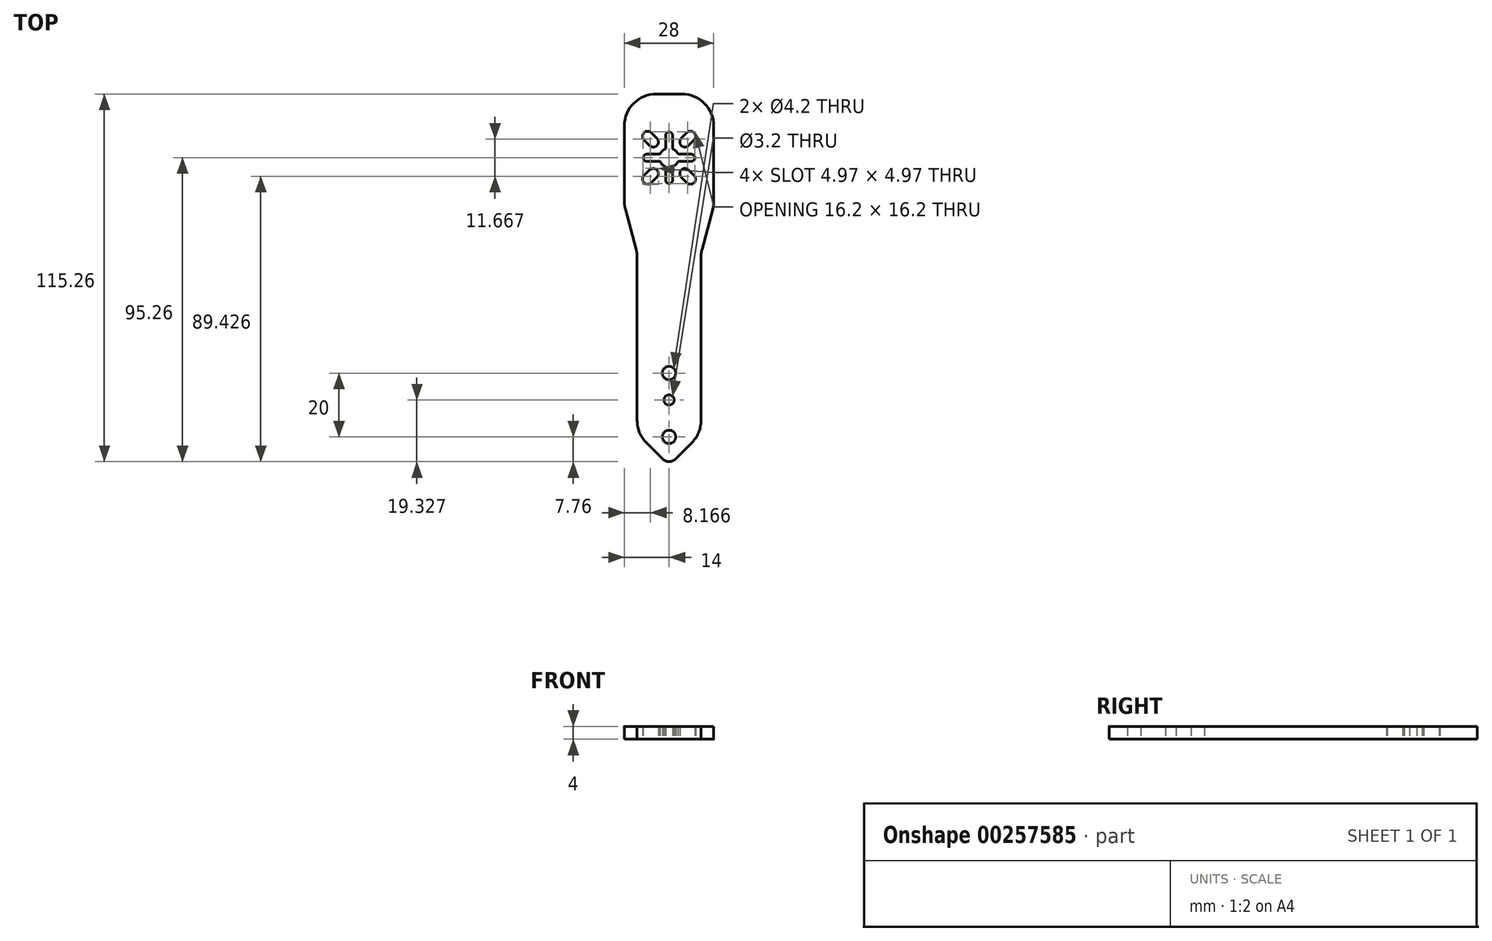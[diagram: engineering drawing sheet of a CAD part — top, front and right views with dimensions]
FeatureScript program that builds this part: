
annotation { "Feature Type Name" : "Feature", "Feature Type Description" : "" }
export const myFeature = defineFeature(function(context is Context, id is Id, definition is map)
    precondition{}
    {
        {
            var Q0;
            Q0=qCreatedBy(makeId("Top.planeOp"),FACE);
            var sketch = newSketch(context, id + "F0", { "sketchPlane" : qUnion([Q0])});
            skLineSegment(sketch, "E0", {"start": v(0, 97.5) * mm, "end": v(0, -97.5) * mm, "construction": true});
            skArc(sketch, "E1", {"start": v(2.8, 98.6) * mm, "mid": v(2.12, 99.62) * mm, "end": v(1.1, 100.3) * mm});
            skCircle(sketch, "E2", {"center": v(0, 10) * mm, "radius": 2.1 * mm});
            skCircle(sketch, "E3", {"center": v(0, 30) * mm, "radius": 2.1 * mm});
            skCircle(sketch, "E4", {"center": v(0, 21.57) * mm, "radius": 1.6 * mm});
            skArc(sketch, "E5", {"start": v(7.85, 103.09) * mm, "mid": v(7.85, 105.35) * mm, "end": v(5.59, 105.35) * mm});
            skArc(sketch, "E6", {"start": v(3.82, 103.58) * mm, "mid": v(3.82, 101.32) * mm, "end": v(6.08, 101.32) * mm});
            skLineSegment(sketch, "E7", {"start": v(5.59, 105.35) * mm, "end": v(3.82, 103.58) * mm});
            skLineSegment(sketch, "E8", {"start": v(7.85, 103.09) * mm, "end": v(6.08, 101.32) * mm});
            skLineSegment(sketch, "E9", {"start": v(0, 97.5) * mm, "end": v(6.72, 104.22) * mm, "construction": true});
            skArc(sketch, "E10", {"start": v(7, 96.4) * mm, "mid": v(8.1, 97.5) * mm, "end": v(7, 98.6) * mm});
            skLineSegment(sketch, "E11", {"start": v(7, 98.6) * mm, "end": v(2.8, 98.6) * mm});
            skLineSegment(sketch, "E12", {"start": v(0, 97.5) * mm, "end": v(7, 97.5) * mm, "construction": true});
            skLineSegment(sketch, "E13.MirrorCS", {"start": v(7, 96.4) * mm, "end": v(2.8, 96.4) * mm});
            skLineSegment(sketch, "E14.1.0", {"start": v(1.1, 104.5) * mm, "end": v(1.1, 100.3) * mm});
            skLineSegment(sketch, "E14.1.1", {"start": v(-1.1, 104.5) * mm, "end": v(-1.1, 100.3) * mm});
            skArc(sketch, "E14.1.2", {"start": v(1.1, 104.5) * mm, "mid": v(0, 105.6) * mm, "end": v(-1.1, 104.5) * mm});
            skArc(sketch, "E14.1.4", {"start": v(-5.59, 105.35) * mm, "mid": v(-7.85, 105.35) * mm, "end": v(-7.85, 103.09) * mm});
            skLineSegment(sketch, "E14.1.5", {"start": v(-7.85, 103.09) * mm, "end": v(-6.08, 101.32) * mm});
            skLineSegment(sketch, "E14.1.6", {"start": v(-5.59, 105.35) * mm, "end": v(-3.82, 103.58) * mm});
            skArc(sketch, "E14.1.7", {"start": v(-6.08, 101.32) * mm, "mid": v(-3.82, 101.32) * mm, "end": v(-3.82, 103.58) * mm});
            skLineSegment(sketch, "E14.2.0", {"start": v(-7, 98.6) * mm, "end": v(-2.8, 98.6) * mm});
            skLineSegment(sketch, "E14.2.1", {"start": v(-7, 96.4) * mm, "end": v(-2.8, 96.4) * mm});
            skArc(sketch, "E14.2.2", {"start": v(-7, 98.6) * mm, "mid": v(-8.1, 97.5) * mm, "end": v(-7, 96.4) * mm});
            skArc(sketch, "E14.2.4", {"start": v(-7.85, 91.91) * mm, "mid": v(-7.85, 89.65) * mm, "end": v(-5.59, 89.65) * mm});
            skLineSegment(sketch, "E14.2.5", {"start": v(-5.59, 89.65) * mm, "end": v(-3.82, 91.42) * mm});
            skLineSegment(sketch, "E14.2.6", {"start": v(-7.85, 91.91) * mm, "end": v(-6.08, 93.68) * mm});
            skArc(sketch, "E14.2.7", {"start": v(-3.82, 91.42) * mm, "mid": v(-3.82, 93.68) * mm, "end": v(-6.08, 93.68) * mm});
            skLineSegment(sketch, "E15.3.3.0", {"start": v(1.1, 90.5) * mm, "end": v(1.1, 94.7) * mm});
            skArc(sketch, "E15.6.3.0", {"start": v(-1.1, 90.5) * mm, "mid": v(0, 89.4) * mm, "end": v(1.1, 90.5) * mm});
            skLineSegment(sketch, "E15.11.3.0", {"start": v(-1.1, 90.5) * mm, "end": v(-1.1, 94.7) * mm});
            skArc(sketch, "E15.13.3.0", {"start": v(5.59, 89.65) * mm, "mid": v(7.85, 89.65) * mm, "end": v(7.85, 91.91) * mm});
            skLineSegment(sketch, "E15.17.3.0", {"start": v(7.85, 91.91) * mm, "end": v(6.08, 93.68) * mm});
            skLineSegment(sketch, "E15.20.3.0", {"start": v(5.59, 89.65) * mm, "end": v(3.82, 91.42) * mm});
            skArc(sketch, "E15.23.3.0", {"start": v(6.08, 93.68) * mm, "mid": v(3.82, 93.68) * mm, "end": v(3.82, 91.42) * mm});
            skArc(sketch, "E16.trimOffspring", {"start": v(-2.8, 96.4) * mm, "mid": v(-2.12, 95.38) * mm, "end": v(-1.1, 94.7) * mm});
            skArc(sketch, "E17.trimOffspring", {"start": v(-1.1, 100.3) * mm, "mid": v(-2.12, 99.62) * mm, "end": v(-2.8, 98.6) * mm});
            skArc(sketch, "E18.trimOffspring", {"start": v(1.1, 94.7) * mm, "mid": v(2.12, 95.38) * mm, "end": v(2.8, 96.4) * mm});
            skLineSegment(sketch, "E19", {"start": v(-10, 11) * mm, "end": v(-10, 67.57) * mm});
            skLineSegment(sketch, "E20", {"start": v(-10, 67.57) * mm, "end": v(-14, 82.5) * mm});
            skLineSegment(sketch, "E21", {"start": v(-14, 82.5) * mm, "end": v(-14, 117.5) * mm});
            skLineSegment(sketch, "E22.MirrorCS", {"start": v(10, 11) * mm, "end": v(10, 67.57) * mm});
            skLineSegment(sketch, "E23.MirrorCS", {"start": v(10, 67.57) * mm, "end": v(14, 82.5) * mm});
            skLineSegment(sketch, "E24.MirrorCS", {"start": v(14, 82.5) * mm, "end": v(14, 117.5) * mm});
            skLineSegment(sketch, "E25", {"start": v(-10, 11) * mm, "end": v(0, 1) * mm});
            skLineSegment(sketch, "E26", {"start": v(10, 11) * mm, "end": v(0, 1) * mm});
            skLineSegment(sketch, "E27", {"start": v(-14, 117.5) * mm, "end": v(14, 117.5) * mm});
            skCircle(sketch, "E28.MirrorC", {"center": v(0, -21.57) * mm, "radius": 1.6 * mm, "construction": true});
            skCircle(sketch, "E29", {"center": v(21.57, 0) * mm, "radius": 1.6 * mm, "construction": true});
            skLineSegment(sketch, "E30", {"start": v(0, 21.57) * mm, "end": v(21.57, 0) * mm, "construction": true});
            skLineSegment(sketch, "E31", {"start": v(21.57, 0) * mm, "end": v(0, -21.57) * mm, "construction": true});
            skSolve(sketch);
        }
        {
            var Q0;
            Q0 = qSketchRegion(id + "F0", true);
            extrude(context, id + "F1", {"entities" : qUnion([Q0]), "depth" : 4 * mm});
        }
        {
            var Q0;
            Q0=makeQuery(id+"F1.opExtrude","SWEPT_EDGE",EDGE,{"disambiguationData":[OSD([sQuery(id+"F0.wireOp",EDGE,"E20"),sQuery(id+"F0.wireOp",EDGE,"E21")])]});
            var Q1;
            Q1=makeQuery(id+"F1.opExtrude","SWEPT_EDGE",EDGE,{"disambiguationData":[OSD([sQuery(id+"F0.wireOp",EDGE,"E19"),sQuery(id+"F0.wireOp",EDGE,"E20")])]});
            var Q2;
            Q2=makeQuery(id+"F1.opExtrude","SWEPT_EDGE",EDGE,{"disambiguationData":[OSD([sQuery(id+"F0.wireOp",EDGE,"E19"),sQuery(id+"F0.wireOp",EDGE,"E25")])]});
            var Q3;
            Q3=makeQuery(id+"F1.opExtrude","SWEPT_EDGE",EDGE,{"disambiguationData":[OSD([sQuery(id+"F0.wireOp",EDGE,"E22.MirrorCS"),sQuery(id+"F0.wireOp",EDGE,"E26")])]});
            var Q4;
            Q4=makeQuery(id+"F1.opExtrude","SWEPT_EDGE",EDGE,{"disambiguationData":[OSD([sQuery(id+"F0.wireOp",EDGE,"E22.MirrorCS"),sQuery(id+"F0.wireOp",EDGE,"E23.MirrorCS")])]});
            var Q5;
            Q5=makeQuery(id+"F1.opExtrude","SWEPT_EDGE",EDGE,{"disambiguationData":[OSD([sQuery(id+"F0.wireOp",EDGE,"E23.MirrorCS"),sQuery(id+"F0.wireOp",EDGE,"E24.MirrorCS")])]});
            var Q6;
            Q6=makeQuery(id+"F1.opExtrude","SWEPT_EDGE",EDGE,{"disambiguationData":[OSD([sQuery(id+"F0.wireOp",EDGE,"E21"),sQuery(id+"F0.wireOp",EDGE,"E27")])]});
            var Q7;
            Q7=makeQuery(id+"F1.opExtrude","SWEPT_EDGE",EDGE,{"disambiguationData":[OSD([sQuery(id+"F0.wireOp",EDGE,"E24.MirrorCS"),sQuery(id+"F0.wireOp",EDGE,"E27")])]});
            fillet(context, id + "F2", {"entities" : qUnion([Q0, Q1, Q2, Q3, Q4, Q5, Q6, Q7]), "radius" : 10 * mm, "tangentPropagation" : true, "allowEdgeOverflow" : false});
        }
        {
            var Q0;
            Q0=makeQuery(id+"F1.opExtrude","SWEPT_EDGE",EDGE,{"disambiguationData":[OSD([sQuery(id+"F0.wireOp",EDGE,"E25"),sQuery(id+"F0.wireOp",EDGE,"E26")])]});
            fillet(context, id + "F3", {"entities" : qUnion([Q0]), "radius" : 3 * mm, "tangentPropagation" : true, "allowEdgeOverflow" : false});
        }
    });
